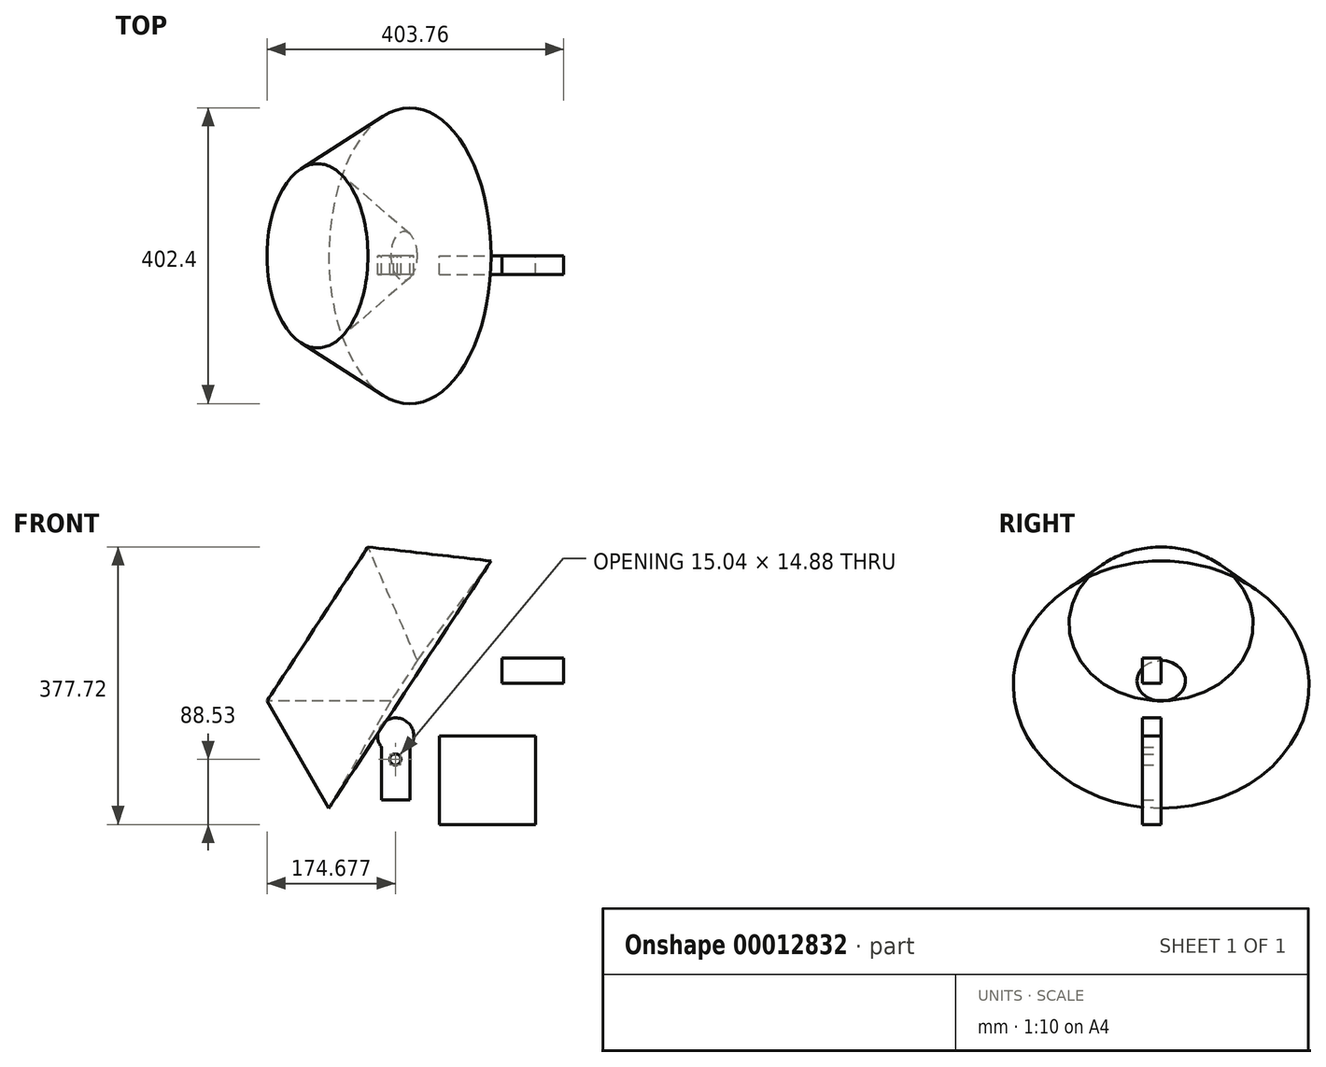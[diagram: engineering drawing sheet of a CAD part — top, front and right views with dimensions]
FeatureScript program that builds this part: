
annotation { "Feature Type Name" : "Feature", "Feature Type Description" : "" }
export const myFeature = defineFeature(function(context is Context, id is Id, definition is map)
    precondition{}
    {
        {
            var Q0;
            Q0=qCreatedBy(makeId("Front.planeOp"),FACE);
            var sketch = newSketch(context, id + "F4", { "sketchPlane" : qUnion([Q0])});
            skLineSegment(sketch, "E0.bottom", {"start": v(63.1, -41.1) * mm, "end": v(24.03, -41.1) * mm});
            skLineSegment(sketch, "E0.left", {"start": v(63.1, -41.1) * mm, "end": v(63.1, 30.6) * mm});
            skLineSegment(sketch, "E0.right", {"start": v(24.03, -41.1) * mm, "end": v(24.03, 30.6) * mm});
            skArc(sketch, "E1", {"start": v(40.67, 21.17) * mm, "mid": v(42.91, 6.3) * mm, "end": v(45.65, 21.09) * mm});
            skArc(sketch, "E2", {"start": v(63.1, 30.6) * mm, "mid": v(43.57, 70.32) * mm, "end": v(24.03, 30.6) * mm});
            skPoint(sketch, "E3.orphan", {"position": v(24.03, 45.66) * mm});
            skPoint(sketch, "E4.orphan", {"position": v(63.1, 45.66) * mm});
            skArc(sketch, "E5.trimOffspring", {"start": v(40.67, 21.17) * mm, "mid": v(43.16, 21) * mm, "end": v(45.65, 21.09) * mm});
            skSolve(sketch);
        }
        {
            var Q0;
            Q0=makeQuery(id+"F4.imprint","IMPRINT",FACE,{"disambiguationData":[TD([[makeQuery(id+"F4.imprint","IMPRINT",EDGE,{"derivedFrom":sQuery(id+"F4.wireOp",EDGE,"E0.bottom")}),-1.0]])]});
            extrude(context, id + "F5", {"entities" : qUnion([Q0]), "depth" : 25.4 * mm});
        }
        {
            var Q0;
            Q0=qCreatedBy(makeId("Front.planeOp"),FACE);
            var sketch = newSketch(context, id + "F0", { "sketchPlane" : qUnion([Q0])});
            skCircle(sketch, "E6.cCircle", {"center": v(-47.42, 44.6) * mm, "radius": 48.64 * mm, "construction": true});
            skLineSegment(sketch, "E6.0", {"start": v(-131.66, 93.24) * mm, "end": v(36.83, 93.24) * mm});
            skLineSegment(sketch, "E6.1", {"start": v(36.83, 93.24) * mm, "end": v(-47.42, -52.67) * mm});
            skLineSegment(sketch, "E6.2", {"start": v(-47.42, -52.67) * mm, "end": v(-131.66, 93.24) * mm});
            skPoint(sketch, "E6.0.midPoint", {"position": v(-47.42, 93.24) * mm});
            skLineSegment(sketch, "E7", {"start": v(32.5, 149.21) * mm, "end": v(68.2, 127.7) * mm, "construction": true});
            skSolve(sketch);
        }
        {
            var Q0;
            Q0=qCreatedBy(makeId("Front.planeOp"),FACE);
            var sketch = newSketch(context, id + "F1", { "sketchPlane" : qUnion([Q0])});
            skLineSegment(sketch, "E8", {"start": v(23.4, 141.49) * mm, "end": v(81.72, 103.25) * mm});
            skSolve(sketch);
        }
        {
            var Q0;
            Q0=makeQuery(id+"F0.imprint","IMPRINT",FACE,{"disambiguationData":[TD([[makeQuery(id+"F0.imprint","IMPRINT",EDGE,{"derivedFrom":sQuery(id+"F0.wireOp",EDGE,"E6.0")}),-1.0]])]});
            var Q1;
            Q1=sQuery(id+"F1.wireOp",EDGE,"E8");
            revolve(context, id + "F6", {"entities" : qUnion([Q0]), "axis" : qUnion([Q1]), "revolveType" : RevolveType.FULL});
        }
        {
            var Q0;
            Q0=qCreatedBy(makeId("Front.planeOp"),FACE);
            var sketch = newSketch(context, id + "F2", { "sketchPlane" : qUnion([Q0])});
            skLineSegment(sketch, "E9.bottom", {"start": v(103.28, -74.8) * mm, "end": v(233.82, -74.8) * mm});
            skLineSegment(sketch, "E9.top", {"start": v(103.28, 45.37) * mm, "end": v(233.82, 45.37) * mm});
            skLineSegment(sketch, "E9.left", {"start": v(103.28, -74.8) * mm, "end": v(103.28, 45.37) * mm});
            skLineSegment(sketch, "E9.right", {"start": v(233.82, -74.8) * mm, "end": v(233.82, 45.37) * mm});
            skLineSegment(sketch, "E10.bottom", {"start": v(187.82, 152.01) * mm, "end": v(272.1, 152.01) * mm});
            skLineSegment(sketch, "E10.top", {"start": v(187.82, 117.56) * mm, "end": v(272.1, 117.56) * mm});
            skLineSegment(sketch, "E10.left", {"start": v(187.82, 152.01) * mm, "end": v(187.82, 117.56) * mm});
            skLineSegment(sketch, "E10.right", {"start": v(272.1, 152.01) * mm, "end": v(272.1, 117.56) * mm});
            skSolve(sketch);
        }
        {
            var Q0;
            Q0=makeQuery(id+"F2.imprint","IMPRINT",FACE,{"disambiguationData":[TD([[makeQuery(id+"F2.imprint","IMPRINT",EDGE,{"derivedFrom":sQuery(id+"F2.wireOp",EDGE,"E10.bottom")}),-1.0]])]});
            var Q1;
            Q1=makeQuery(id+"F2.imprint","IMPRINT",FACE,{"disambiguationData":[TD([[makeQuery(id+"F2.imprint","IMPRINT",EDGE,{"derivedFrom":sQuery(id+"F2.wireOp",EDGE,"E9.bottom")}),1.0]])]});
            extrude(context, id + "F7", {"entities" : qUnion([Q0, Q1]), "depth" : 25.4 * mm});
        }
    });
